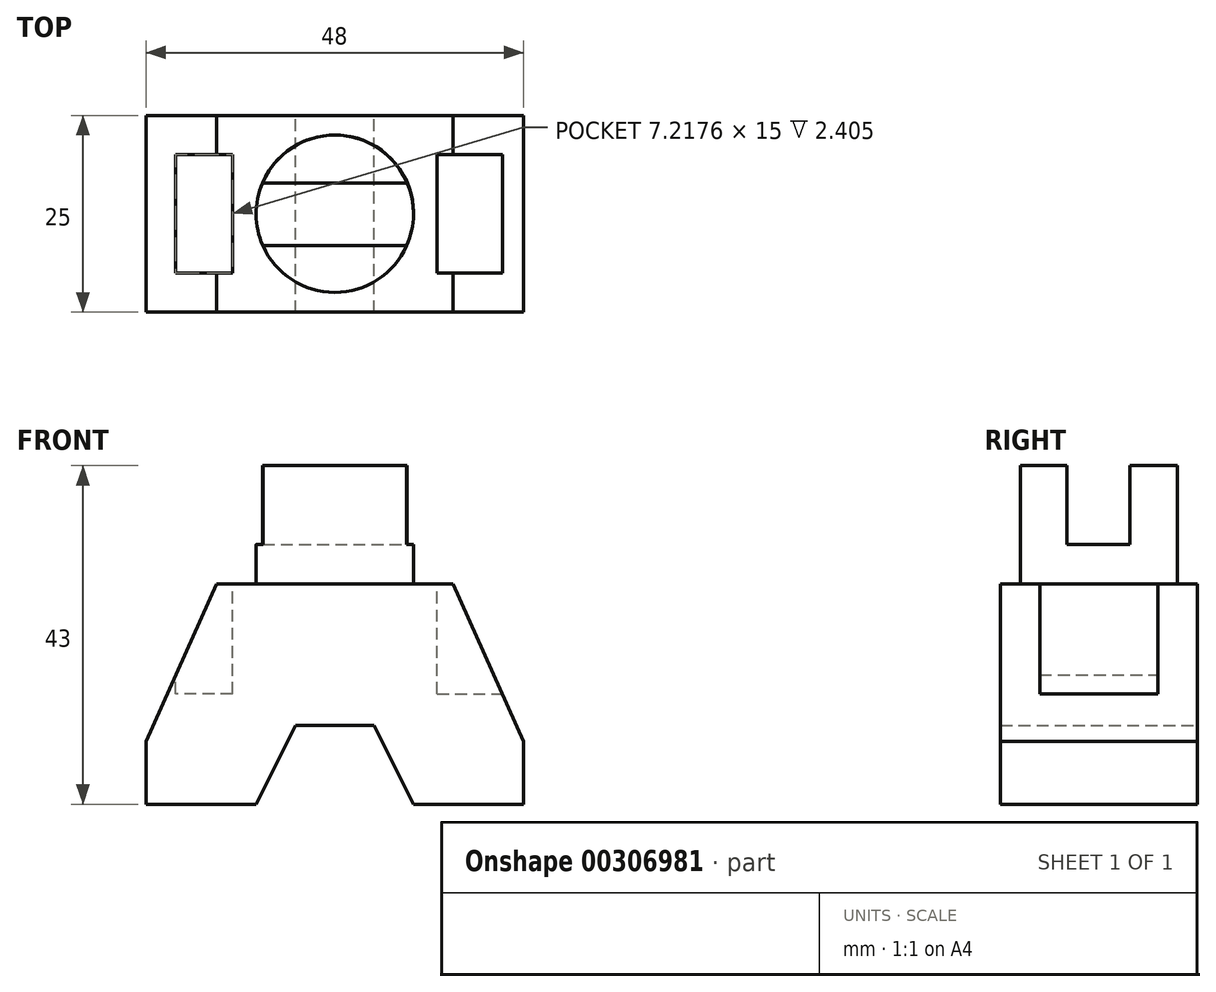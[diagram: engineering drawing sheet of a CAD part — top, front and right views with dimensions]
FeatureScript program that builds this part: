
annotation { "Feature Type Name" : "Feature", "Feature Type Description" : "" }
export const myFeature = defineFeature(function(context is Context, id is Id, definition is map)
    precondition{}
    {
        {
            var Q0;
            Q0=qCreatedBy(makeId("Front.planeOp"),FACE);
            var sketch = newSketch(context, id + "F0", { "sketchPlane" : qUnion([Q0])});
            skLineSegment(sketch, "E0", {"start": v(24, -28) * mm, "end": v(24, -20) * mm});
            skLineSegment(sketch, "E1", {"start": v(24, -20) * mm, "end": v(15, 0) * mm});
            skLineSegment(sketch, "E2", {"start": v(15, 0) * mm, "end": v(-15, 0) * mm});
            skLineSegment(sketch, "E3", {"start": v(-15, 0) * mm, "end": v(-24, -20) * mm});
            skLineSegment(sketch, "E4", {"start": v(-24, -20) * mm, "end": v(-24, -28) * mm});
            skLineSegment(sketch, "E5", {"start": v(-24, -28) * mm, "end": v(-10, -28) * mm});
            skLineSegment(sketch, "E6", {"start": v(-10, -28) * mm, "end": v(-5, -18) * mm});
            skLineSegment(sketch, "E7", {"start": v(-5, -18) * mm, "end": v(5, -18) * mm});
            skLineSegment(sketch, "E8", {"start": v(5, -18) * mm, "end": v(10, -28) * mm});
            skLineSegment(sketch, "E9", {"start": v(10, -28) * mm, "end": v(24, -28) * mm});
            skSolve(sketch);
        }
        {
            var Q0;
            Q0=makeQuery(id+"F0.imprint","IMPRINT",FACE,{"disambiguationData":[TD([[makeQuery(id+"F0.imprint","IMPRINT",EDGE,{"derivedFrom":sQuery(id+"F0.wireOp",EDGE,"E0")}),1.0]])]});
            extrude(context, id + "F1", {"entities" : qUnion([Q0]), "depth" : 25 * mm});
        }
        {
            var Q0;
            Q0=makeQuery(id+"F1.opExtrude","SWEPT_FACE",FACE,{"disambiguationData":[OSD([sQuery(id+"F0.wireOp",EDGE,"E3")])]});
            var sketch = newSketch(context, id + "F2", { "sketchPlane" : qUnion([Q0])});
            skLineSegment(sketch, "E10", {"start": v(5, -6.16) * mm, "end": v(5, -20.16) * mm});
            skLineSegment(sketch, "E11", {"start": v(5, -20.16) * mm, "end": v(20, -20.16) * mm});
            skLineSegment(sketch, "E12", {"start": v(20, -20.16) * mm, "end": v(20, -6.16) * mm});
            skSolve(sketch);
        }
        {
            var Q0;
            Q0=makeQuery(id+"F1.opExtrude","SWEPT_FACE",FACE,{"disambiguationData":[OSD([sQuery(id+"F0.wireOp",EDGE,"E2")])]});
            var sketch = newSketch(context, id + "F3", { "sketchPlane" : qUnion([Q0])});
            skLineSegment(sketch, "E13.bottom", {"start": v(-13, -5) * mm, "end": v(-20.22, -5) * mm});
            skLineSegment(sketch, "E13.top", {"start": v(-13, -20) * mm, "end": v(-20.22, -20) * mm});
            skLineSegment(sketch, "E13.left", {"start": v(-13, -5) * mm, "end": v(-13, -20) * mm});
            skLineSegment(sketch, "E13.right", {"start": v(-20.22, -5) * mm, "end": v(-20.22, -20) * mm});
            skSolve(sketch);
        }
        {
            var Q0;
            {var subQ0=sQuery(id+"F3.wireOp",EDGE,"E13.left");Q0=makeQuery(id+"F3.imprint","IMPRINT",FACE,{"disambiguationData":[TD([[makeQuery(id+"F3.imprint","IMPRINT",EDGE,{"derivedFrom":subQ0}),-1.0]])]});}
            var Q1;
            {var subQ0=sQuery(id+"F3.wireOp",EDGE,"E13.right");Q1=makeQuery(id+"F3.imprint","IMPRINT",FACE,{"disambiguationData":[TD([[makeQuery(id+"F3.imprint","IMPRINT",EDGE,{"derivedFrom":subQ0}),1.0]])]});}
            extrude(context, id + "F4", {"entities" : qUnion([Q0, Q1]), "operationType" : NewBodyOperationType.REMOVE, "oppositeDirection" : true, "depth" : 14 * mm});
        }
        {
            var Q0;
            Q0=makeQuery(id+"F1.opExtrude","SWEPT_FACE",FACE,{"disambiguationData":[OSD([sQuery(id+"F0.wireOp",EDGE,"E2")])]});
            var sketch = newSketch(context, id + "F5", { "sketchPlane" : qUnion([Q0])});
            skLineSegment(sketch, "E14.bottom", {"start": v(13, -5) * mm, "end": v(21.93, -5) * mm});
            skLineSegment(sketch, "E14.top", {"start": v(13, -20) * mm, "end": v(21.93, -20) * mm});
            skLineSegment(sketch, "E14.left", {"start": v(13, -5) * mm, "end": v(13, -20) * mm});
            skLineSegment(sketch, "E14.right", {"start": v(21.93, -5) * mm, "end": v(21.93, -20) * mm});
            skSolve(sketch);
        }
        {
            var Q0;
            {var subQ0=sQuery(id+"F5.wireOp",EDGE,"E14.right");Q0=makeQuery(id+"F5.imprint","IMPRINT",FACE,{"disambiguationData":[TD([[makeQuery(id+"F5.imprint","IMPRINT",EDGE,{"derivedFrom":subQ0}),-1.0]])]});}
            var Q1;
            {var subQ0=sQuery(id+"F5.wireOp",EDGE,"E14.left");Q1=makeQuery(id+"F5.imprint","IMPRINT",FACE,{"disambiguationData":[TD([[makeQuery(id+"F5.imprint","IMPRINT",EDGE,{"derivedFrom":subQ0}),1.0]])]});}
            extrude(context, id + "F6", {"entities" : qUnion([Q0, Q1]), "operationType" : NewBodyOperationType.REMOVE, "oppositeDirection" : true, "depth" : 14 * mm});
        }
        {
            var Q0;
            Q0=makeQuery(id+"F1.opExtrude","SWEPT_FACE",FACE,{"disambiguationData":[OSD([sQuery(id+"F0.wireOp",EDGE,"E2")])]});
            var sketch = newSketch(context, id + "F7", { "sketchPlane" : qUnion([Q0])});
            skCircle(sketch, "E15", {"center": v(0, -12.5) * mm, "radius": 10 * mm});
            skSolve(sketch);
        }
        {
            var Q0;
            Q0 = qSketchRegion(id + "F7", true);
            extrude(context, id + "F8", {"entities" : qUnion([Q0]), "operationType" : NewBodyOperationType.ADD, "depth" : 15 * mm});
        }
        {
            var Q0;
            Q0=makeQuery(id+"F8.opExtrude","CAP_FACE",FACE,{"disambiguationData":[OSD([sQuery(id+"F7.wireOp",EDGE,"E15")])],"isStart":false});
            var sketch = newSketch(context, id + "F9", { "sketchPlane" : qUnion([Q0])});
            skLineSegment(sketch, "E16.bottom", {"start": v(-10, -8.57) * mm, "end": v(10, -8.57) * mm});
            skLineSegment(sketch, "E16.top", {"start": v(-10, -16.57) * mm, "end": v(10, -16.57) * mm});
            skLineSegment(sketch, "E16.left", {"start": v(-10, -8.57) * mm, "end": v(-10, -16.57) * mm});
            skLineSegment(sketch, "E16.right", {"start": v(10, -8.57) * mm, "end": v(10, -16.57) * mm});
            skSolve(sketch);
        }
        {
            var Q0;
            {var subQ0=sQuery(id+"F9.wireOp",EDGE,"E16.bottom");var subQ1=makeQuery(id+"F8.opExtrude","CAP_EDGE",EDGE,{"disambiguationData":[OSD([sQuery(id+"F7.wireOp",EDGE,"E15")])],"isStart":false});var subQ4=makeQuery(id+"F9.imprint","INTERSECT",VERTEX,{"disambiguationData":[OD(0.0)],"derivedFrom":[subQ1,subQ0]});Q0=makeQuery(id+"F9.imprint","IMPRINT",FACE,{"disambiguationData":[TD([[makeQuery(id+"F9.imprint","IMPRINT",EDGE,{"disambiguationData":[TD([[subQ4,-1.0]])],"derivedFrom":subQ0}),-1.0]])]});}
            extrude(context, id + "F10", {"entities" : qUnion([Q0]), "operationType" : NewBodyOperationType.REMOVE, "oppositeDirection" : true, "depth" : 10 * mm});
        }
    });
